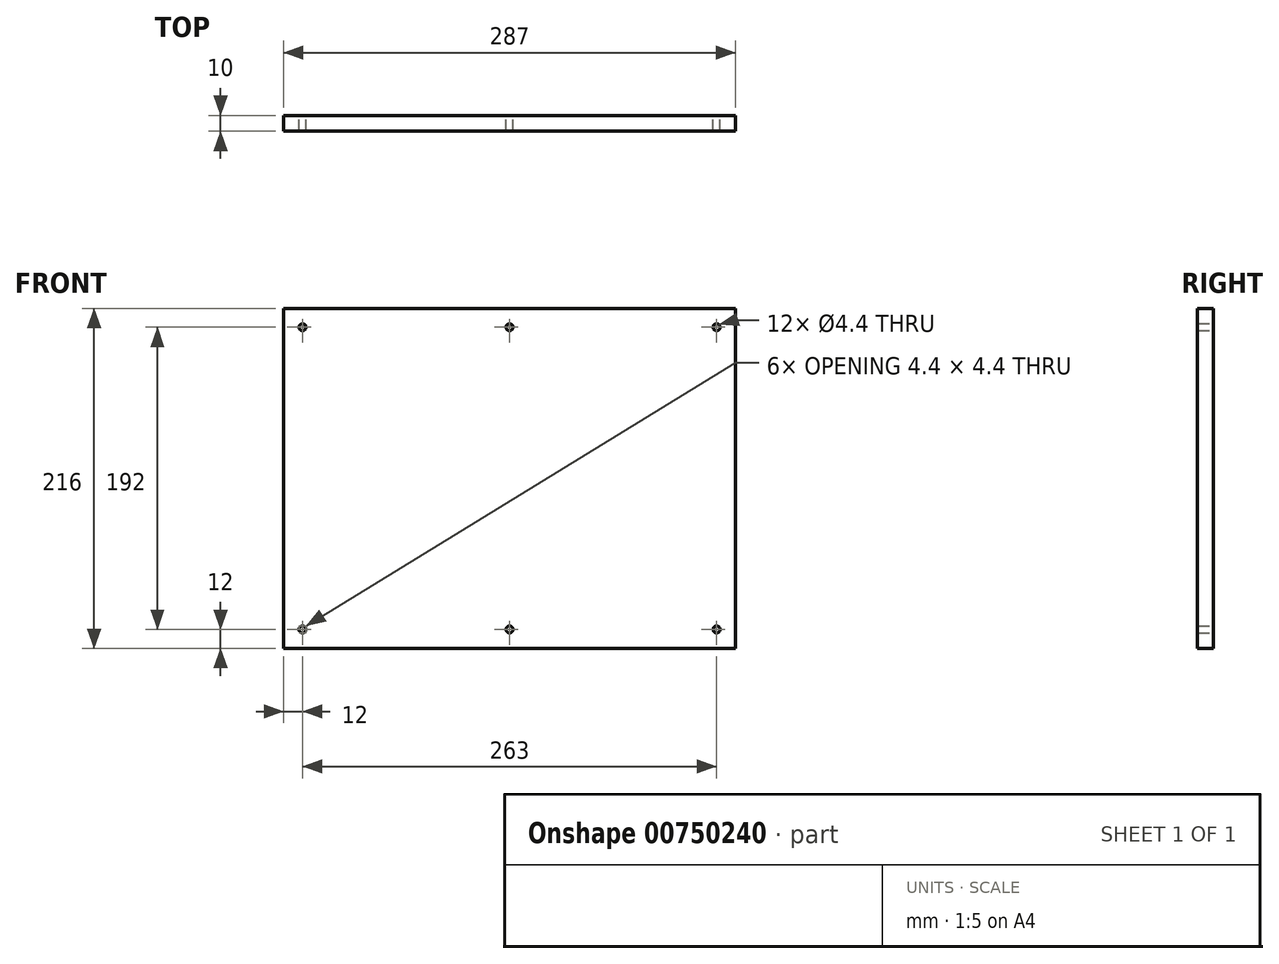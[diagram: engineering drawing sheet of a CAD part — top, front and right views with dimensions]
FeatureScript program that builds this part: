
annotation { "Feature Type Name" : "Feature", "Feature Type Description" : "" }
export const myFeature = defineFeature(function(context is Context, id is Id, definition is map)
    precondition{}
    {
        {
            var Q0;
            Q0=qCreatedBy(makeId("Front.planeOp"),FACE);
            var sketch = newSketch(context, id + "F0", { "sketchPlane" : qUnion([Q0])});
            skLineSegment(sketch, "E0.bottom", {"start": v(143.5, -108) * mm, "end": v(-143.5, -108) * mm});
            skLineSegment(sketch, "E0.top", {"start": v(143.5, 108) * mm, "end": v(-143.5, 108) * mm});
            skLineSegment(sketch, "E0.left", {"start": v(143.5, -108) * mm, "end": v(143.5, 108) * mm});
            skLineSegment(sketch, "E0.right", {"start": v(-143.5, -108) * mm, "end": v(-143.5, 108) * mm});
            skPoint(sketch, "E0.middle", {"position": v(0, 0) * mm});
            skLineSegment(sketch, "E1.bottom", {"start": v(131.5, -96) * mm, "end": v(-131.5, -96) * mm, "construction": true});
            skLineSegment(sketch, "E1.top", {"start": v(131.5, 96) * mm, "end": v(-131.5, 96) * mm, "construction": true});
            skLineSegment(sketch, "E1.left", {"start": v(131.5, -96) * mm, "end": v(131.5, 96) * mm, "construction": true});
            skLineSegment(sketch, "E1.right", {"start": v(-131.5, -96) * mm, "end": v(-131.5, 96) * mm, "construction": true});
            skPoint(sketch, "E2", {"position": v(0, 96) * mm});
            skPoint(sketch, "E3", {"position": v(0, -96) * mm});
            skSolve(sketch);
        }
        {
            var Q0;
            Q0=makeQuery(id+"F0.imprint","IMPRINT",FACE,{"disambiguationData":[TD([[makeQuery(id+"F0.imprint","IMPRINT",EDGE,{"derivedFrom":sQuery(id+"F0.wireOp",EDGE,"E0.bottom")}),-1.0]])]});
            extrude(context, id + "F1", {"entities" : qUnion([Q0]), "depth" : 10 * mm, "offsetDistance" : 25 * mm});
        }
        {
            var Q0;
            Q0=sQuery(id+"F0.wireOp",VERTEX,"E2");
            var Q1;
            Q1=sQuery(id+"F0.wireOp",VERTEX,"E1.right.end");
            var Q2;
            Q2=sQuery(id+"F0.wireOp",VERTEX,"E1.left.end");
            var Q3;
            Q3=sQuery(id+"F0.wireOp",VERTEX,"E1.left.start");
            var Q4;
            Q4=sQuery(id+"F0.wireOp",VERTEX,"E1.right.start");
            var Q5;
            Q5=sQuery(id+"F0.wireOp",VERTEX,"E3");
            var Q6;
            Q6=makeQuery(id+"F1.opExtrude","SWEPT_BODY",BODY,{"disambiguationData":[OSD([sQuery(id+"F0.wireOp",EDGE,"E0.bottom"),sQuery(id+"F0.wireOp",EDGE,"E0.top"),sQuery(id+"F0.wireOp",EDGE,"E0.left"),sQuery(id+"F0.wireOp",EDGE,"E0.right")])]});
            hole(context, id + "F2", {"style" : HoleStyle.SIMPLE, "endStyle" : HoleEndStyle.THROUGH, "oppositeDirection" : true, "standardTappedOrClearance" : lookupTablePath({ "standard" : "ISO", "fit" : "Normal", "size" : "M4", "type" : "Clearance" }), "standardBlindInLast" : lookupTablePath({ "fit" : "Standard", "standard" : "ISO", "size" : "M4", "type" : "Clearance" }), "holeDiameter" : 4.4 * mm, "majorDiameter" : 5 * mm, "isTappedThrough" : true, "tappedDepth" : 12 * mm, "tapClearance" : 3, "locations" : qUnion([Q0, Q1, Q2, Q3, Q4, Q5]), "scope" : qUnion([Q6])});
        }
    });
